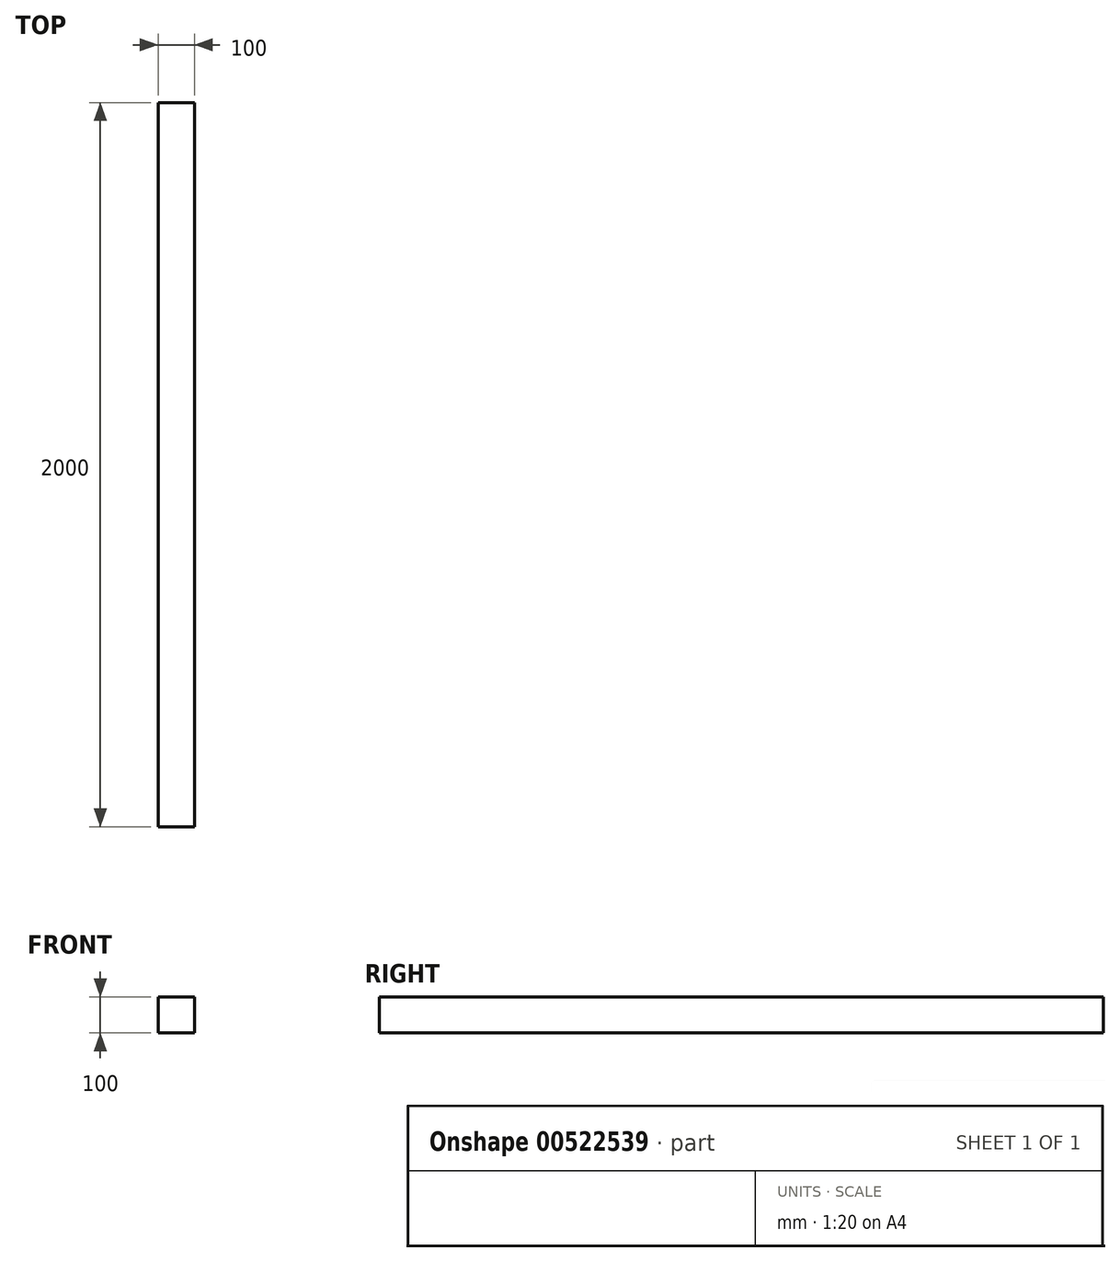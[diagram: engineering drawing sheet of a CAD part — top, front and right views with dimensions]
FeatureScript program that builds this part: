
annotation { "Feature Type Name" : "Feature", "Feature Type Description" : "" }
export const myFeature = defineFeature(function(context is Context, id is Id, definition is map)
    precondition{}
    {
        {
            var Q0;
            Q0=qCreatedBy(makeId("Front.planeOp"),FACE);
            var sketch = newSketch(context, id + "F0", { "sketchPlane" : qUnion([Q0])});
            skLineSegment(sketch, "E0.bottom", {"start": v(-118.75, 94.8) * mm, "end": v(-18.75, 94.8) * mm});
            skLineSegment(sketch, "E0.top", {"start": v(-118.75, -5.2) * mm, "end": v(-18.75, -5.2) * mm});
            skLineSegment(sketch, "E0.left", {"start": v(-118.75, 94.8) * mm, "end": v(-118.75, -5.2) * mm});
            skLineSegment(sketch, "E0.right", {"start": v(-18.75, 94.8) * mm, "end": v(-18.75, -5.2) * mm});
            skSolve(sketch);
        }
        {
            var Q0;
            Q0=qSketchRegion(id+"F0",true);
            extrude(context, id + "F1", {"entities" : qUnion([Q0]), "depth" : 2000 * mm, "offsetDistance" : 25 * mm});
        }
    });
